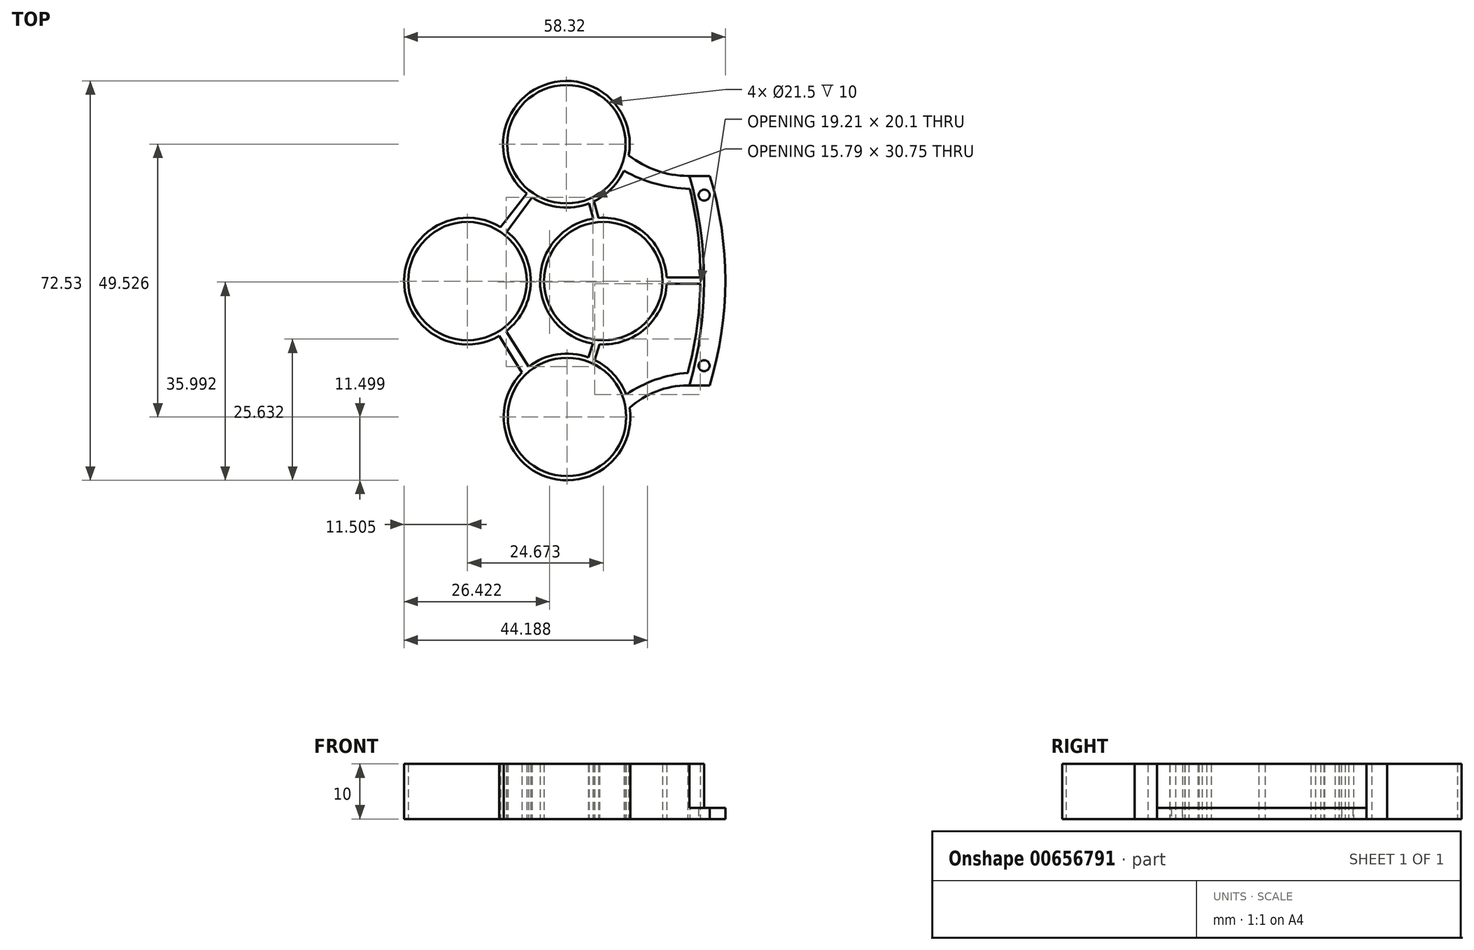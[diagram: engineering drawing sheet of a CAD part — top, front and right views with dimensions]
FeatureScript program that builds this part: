
annotation { "Feature Type Name" : "Feature", "Feature Type Description" : "" }
export const myFeature = defineFeature(function(context is Context, id is Id, definition is map)
    precondition{}
    {
        {
            var Q0;
            Q0=qCreatedBy(makeId("Top.planeOp"),FACE);
            var sketch = newSketch(context, id + "F0", { "sketchPlane" : qUnion([Q0])});
            skCircle(sketch, "E0", {"center": v(0, 0) * mm, "radius": 65 * mm, "construction": true});
            skCircle(sketch, "E1", {"center": v(0, 0) * mm, "radius": 49.4 * mm, "construction": true});
            skCircle(sketch, "E2", {"center": v(42.7, 24.86) * mm, "radius": 10.75 * mm});
            skCircle(sketch, "E3", {"center": v(42.8, -24.67) * mm, "radius": 10.75 * mm});
            skCircle(sketch, "E4", {"center": v(49.4, 0) * mm, "radius": 10.75 * mm});
            skCircle(sketch, "E5", {"center": v(0, 0) * mm, "radius": 24.73 * mm, "construction": true});
            skLineSegment(sketch, "E6", {"start": v(0, 0) * mm, "end": v(95.97, 0) * mm, "construction": true});
            skLineSegment(sketch, "E7", {"start": v(0, 0) * mm, "end": v(-94.56, 0) * mm, "construction": true});
            skCircle(sketch, "E8", {"center": v(24.73, 0) * mm, "radius": 10.75 * mm});
            skLineSegment(sketch, "E9", {"start": v(-89.55, 88.06) * mm, "end": v(89.42, 88.01) * mm, "construction": true});
            skCircle(sketch, "E10", {"center": v(67.7, -15.36) * mm, "radius": 1 * mm});
            skCircle(sketch, "E11", {"center": v(67.72, 15.61) * mm, "radius": 1 * mm});
            skCircle(sketch, "E12", {"center": v(24.73, 0) * mm, "radius": 11.5 * mm});
            skCircle(sketch, "E13", {"center": v(42.7, 24.86) * mm, "radius": 11.5 * mm});
            skCircle(sketch, "E14", {"center": v(49.4, 0) * mm, "radius": 11.5 * mm});
            skCircle(sketch, "E15", {"center": v(42.8, -24.67) * mm, "radius": 11.5 * mm});
            skLineSegment(sketch, "E16", {"start": v(36.22, 0.57) * mm, "end": v(37.92, 0.57) * mm});
            skLineSegment(sketch, "E17", {"start": v(37.92, -0.51) * mm, "end": v(36.22, -0.51) * mm});
            skLineSegment(sketch, "E18", {"start": v(46.8, 14.11) * mm, "end": v(47.55, 11.35) * mm});
            skLineSegment(sketch, "E19", {"start": v(48.51, 11.47) * mm, "end": v(47.7, 14.5) * mm});
            skLineSegment(sketch, "E20", {"start": v(47.5, -11.34) * mm, "end": v(46.68, -13.84) * mm});
            skLineSegment(sketch, "E21", {"start": v(48.7, -11.48) * mm, "end": v(47.81, -14.32) * mm});
            skLineSegment(sketch, "E22", {"start": v(34.64, -16.57) * mm, "end": v(30.5, -9.95) * mm});
            skLineSegment(sketch, "E23", {"start": v(31.76, -9.1) * mm, "end": v(35.8, -15.55) * mm});
            skLineSegment(sketch, "E24", {"start": v(36.46, 15.2) * mm, "end": v(31.9, 9) * mm});
            skLineSegment(sketch, "E25", {"start": v(35.5, 15.89) * mm, "end": v(30.74, 9.8) * mm});
            skArc(sketch, "E26", {"start": v(68.7, -18.96) * mm, "mid": v(71.55, 0.07) * mm, "end": v(68.75, 19.11) * mm});
            skLineSegment(sketch, "E27", {"start": v(68.7, -18.96) * mm, "end": v(64.7, -18.96) * mm});
            skLineSegment(sketch, "E28", {"start": v(68.75, 19.11) * mm, "end": v(64.75, 19.11) * mm});
            skArc(sketch, "E29", {"start": v(54.02, 22.84) * mm, "mid": v(59.07, 20.07) * mm, "end": v(64.75, 19.11) * mm});
            skArc(sketch, "E30", {"start": v(64.7, -18.96) * mm, "mid": v(59.07, -20) * mm, "end": v(54.19, -23.02) * mm});
            skArc(sketch, "E31", {"start": v(64.75, -16.64) * mm, "mid": v(67.03, 0.04) * mm, "end": v(65.1, 16.76) * mm});
            skArc(sketch, "E32", {"start": v(64.75, -16.64) * mm, "mid": v(58.9, -17.9) * mm, "end": v(53.56, -20.59) * mm});
            skArc(sketch, "E33", {"start": v(53.14, 20.04) * mm, "mid": v(58.93, 17.67) * mm, "end": v(65.1, 16.76) * mm});
            skLineSegment(sketch, "E34", {"start": v(67.03, 0.67) * mm, "end": v(60.89, 0.67) * mm});
            skLineSegment(sketch, "E35", {"start": v(60.9, -0.49) * mm, "end": v(67.02, -0.49) * mm});
            skSolve(sketch);
        }
        {
            var Q0;
            Q0 = qSketchRegion(id + "F0", true);
            var Q1;
            {var subQ0=sQuery(id+"F0.wireOp",EDGE,"E34");Q1=makeQuery(id+"F0.imprint","IMPRINT",FACE,{"disambiguationData":[TD([[makeQuery(id+"F0.imprint","IMPRINT",EDGE,{"derivedFrom":subQ0}),1.0]])]});}
            var Q2;
            Q2=makeQuery(id+"F0.imprint","IMPRINT",FACE,{"disambiguationData":[TD([[makeQuery(id+"F0.imprint","IMPRINT",EDGE,{"derivedFrom":sQuery(id+"F0.wireOp",EDGE,"E4")}),-1.0]])]});
            var Q3;
            {var subQ0=sQuery(id+"F0.wireOp",EDGE,"E20");Q3=makeQuery(id+"F0.imprint","IMPRINT",FACE,{"disambiguationData":[TD([[makeQuery(id+"F0.imprint","IMPRINT",EDGE,{"derivedFrom":subQ0}),1.0]])]});}
            var Q4;
            {var subQ0=sQuery(id+"F0.wireOp",EDGE,"E18");Q4=makeQuery(id+"F0.imprint","IMPRINT",FACE,{"disambiguationData":[TD([[makeQuery(id+"F0.imprint","IMPRINT",EDGE,{"derivedFrom":subQ0}),1.0]])]});}
            extrude(context, id + "F1", {"entities" : qUnion([Q0, Q1, Q2, Q3, Q4]), "depth" : 10 * mm, "offsetDistance" : 25 * mm});
        }
        {
            var Q0;
            Q0=makeQuery(id+"F1.opExtrude","CAP_FACE",FACE,{"disambiguationData":[OSD([sQuery(id+"F0.wireOp",EDGE,"E2"),sQuery(id+"F0.wireOp",EDGE,"E3"),sQuery(id+"F0.wireOp",EDGE,"E4"),sQuery(id+"F0.wireOp",EDGE,"E8"),sQuery(id+"F0.wireOp",EDGE,"E10"),sQuery(id+"F0.wireOp",EDGE,"E11"),sQuery(id+"F0.wireOp",EDGE,"E12"),sQuery(id+"F0.wireOp",EDGE,"E13"),sQuery(id+"F0.wireOp",EDGE,"E14"),sQuery(id+"F0.wireOp",EDGE,"E15"),sQuery(id+"F0.wireOp",EDGE,"E18"),sQuery(id+"F0.wireOp",EDGE,"E19"),sQuery(id+"F0.wireOp",EDGE,"E20"),sQuery(id+"F0.wireOp",EDGE,"E21"),sQuery(id+"F0.wireOp",EDGE,"E22"),sQuery(id+"F0.wireOp",EDGE,"E23"),sQuery(id+"F0.wireOp",EDGE,"E24"),sQuery(id+"F0.wireOp",EDGE,"E25"),sQuery(id+"F0.wireOp",EDGE,"E26"),sQuery(id+"F0.wireOp",EDGE,"E27"),sQuery(id+"F0.wireOp",EDGE,"E28"),sQuery(id+"F0.wireOp",EDGE,"E29"),sQuery(id+"F0.wireOp",EDGE,"E30"),sQuery(id+"F0.wireOp",EDGE,"E31"),sQuery(id+"F0.wireOp",EDGE,"E32"),sQuery(id+"F0.wireOp",EDGE,"E33"),sQuery(id+"F0.wireOp",EDGE,"E34"),sQuery(id+"F0.wireOp",EDGE,"E35")])],"isStart":false});
            var sketch = newSketch(context, id + "F2", { "sketchPlane" : qUnion([Q0])});
            skArc(sketch, "E36", {"start": v(64.85, -19.72) * mm, "mid": v(67.68, 0.27) * mm, "end": v(64.7, 20.24) * mm});
            skLineSegment(sketch, "E37", {"start": v(64.7, 20.24) * mm, "end": v(70.53, 20.24) * mm});
            skLineSegment(sketch, "E38", {"start": v(70.53, 20.24) * mm, "end": v(72.69, -0.84) * mm});
            skLineSegment(sketch, "E39", {"start": v(72.69, -0.84) * mm, "end": v(72.1, -18.96) * mm});
            skLineSegment(sketch, "E40", {"start": v(64.85, -19.72) * mm, "end": v(72.1, -18.96) * mm});
            skSolve(sketch);
        }
        {
            var Q0;
            Q0 = qSketchRegion(id + "F2", true);
            extrude(context, id + "F3", {"entities" : qUnion([Q0]), "operationType" : NewBodyOperationType.REMOVE, "oppositeDirection" : true, "depth" : 8 * mm, "offsetDistance" : 25 * mm});
        }
    });
